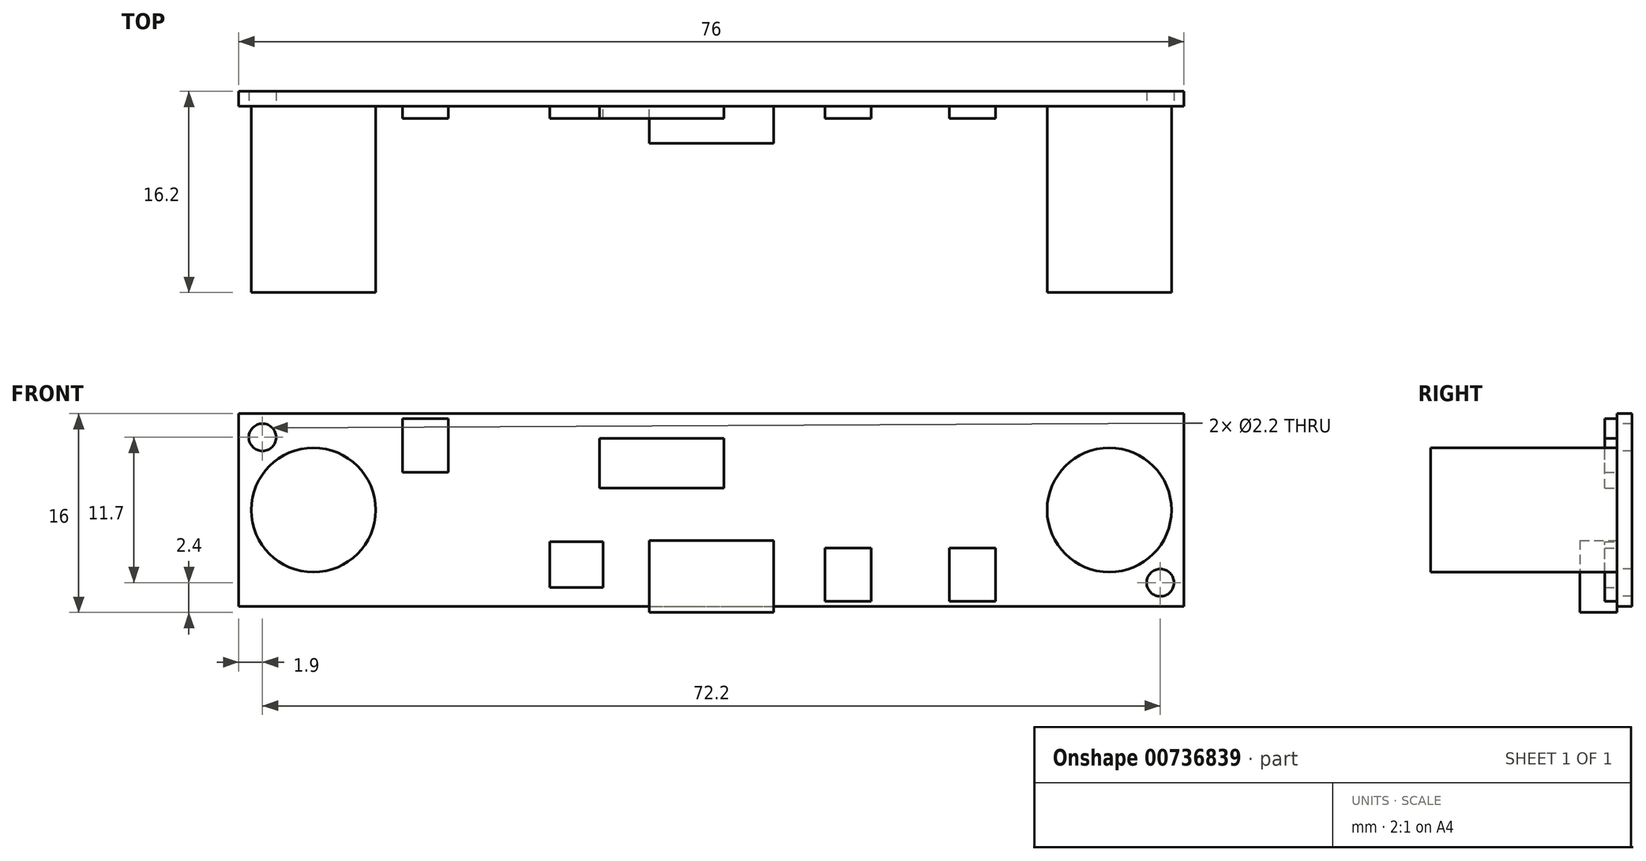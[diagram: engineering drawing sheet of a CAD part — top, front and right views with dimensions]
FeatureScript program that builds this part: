
annotation { "Feature Type Name" : "Feature", "Feature Type Description" : "" }
export const myFeature = defineFeature(function(context is Context, id is Id, definition is map)
    precondition{}
    {
        {
            var Q0;
            Q0=qCreatedBy(makeId("Front.planeOp"),FACE);
            var sketch = newSketch(context, id + "F0", { "sketchPlane" : qUnion([Q0])});
            skLineSegment(sketch, "E0.bottom", {"start": v(-38, 7.75) * mm, "end": v(38, 7.75) * mm});
            skLineSegment(sketch, "E0.top", {"start": v(-38, -7.75) * mm, "end": v(38, -7.75) * mm});
            skLineSegment(sketch, "E0.left", {"start": v(-38, 7.75) * mm, "end": v(-38, -7.75) * mm});
            skLineSegment(sketch, "E0.right", {"start": v(38, 7.75) * mm, "end": v(38, -7.75) * mm});
            skPoint(sketch, "E0.middle", {"position": v(0, 0) * mm});
            skCircle(sketch, "E1", {"center": v(36.1, -5.85) * mm, "radius": 1.1 * mm});
            skCircle(sketch, "E2.1.1", {"center": v(-36.1, 5.85) * mm, "radius": 1.1 * mm});
            skSolve(sketch);
        }
        {
            var Q0;
            Q0=qSketchRegion(id+"F0",true);
            extrude(context, id + "F1", {"entities" : qUnion([Q0]), "oppositeDirection" : true, "depth" : 1.2 * mm});
        }
        {
            var Q0;
            Q0=qCreatedBy(makeId("Front.planeOp"),FACE);
            var sketch = newSketch(context, id + "F2", { "sketchPlane" : qUnion([Q0])});
            skLineSegment(sketch, "E3.bottom", {"start": v(-38, 7.75) * mm, "end": v(38, 7.75) * mm, "construction": true});
            skLineSegment(sketch, "E3.top", {"start": v(-38, -7.75) * mm, "end": v(38, -7.75) * mm, "construction": true});
            skLineSegment(sketch, "E3.left", {"start": v(-38, 7.75) * mm, "end": v(-38, -7.75) * mm, "construction": true});
            skLineSegment(sketch, "E3.right", {"start": v(38, 7.75) * mm, "end": v(38, -7.75) * mm, "construction": true});
            skPoint(sketch, "E3.middle", {"position": v(0, 0) * mm});
            skPoint(sketch, "E4.middle", {"position": v(0, -7.75) * mm});
            skLineSegment(sketch, "E5.bottom", {"start": v(12.85, -7.35) * mm, "end": v(9.15, -7.35) * mm});
            skLineSegment(sketch, "E5.top", {"start": v(12.85, -3.05) * mm, "end": v(9.15, -3.05) * mm});
            skLineSegment(sketch, "E5.left", {"start": v(12.85, -7.35) * mm, "end": v(12.85, -3.05) * mm});
            skLineSegment(sketch, "E5.right", {"start": v(9.15, -7.35) * mm, "end": v(9.15, -3.05) * mm});
            skPoint(sketch, "E5.middle", {"position": v(11, -5.2) * mm});
            skLineSegment(sketch, "E6.bottom", {"start": v(-21.15, 3.05) * mm, "end": v(-24.85, 3.05) * mm});
            skLineSegment(sketch, "E6.top", {"start": v(-21.15, 7.35) * mm, "end": v(-24.85, 7.35) * mm});
            skLineSegment(sketch, "E6.left", {"start": v(-21.15, 3.05) * mm, "end": v(-21.15, 7.35) * mm});
            skLineSegment(sketch, "E6.right", {"start": v(-24.85, 3.05) * mm, "end": v(-24.85, 7.35) * mm});
            skPoint(sketch, "E6.middle", {"position": v(-23, 5.2) * mm});
            skLineSegment(sketch, "E7", {"start": v(16, 2.67) * mm, "end": v(16, -12) * mm, "construction": true});
            skLineSegment(sketch, "E8.MirrorCS", {"start": v(19.15, -7.35) * mm, "end": v(19.15, -3.05) * mm});
            skLineSegment(sketch, "E9.MirrorCS", {"start": v(19.15, -3.05) * mm, "end": v(22.85, -3.05) * mm});
            skLineSegment(sketch, "E10.MirrorCS", {"start": v(22.85, -7.35) * mm, "end": v(22.85, -3.05) * mm});
            skLineSegment(sketch, "E11.MirrorCS", {"start": v(19.15, -7.35) * mm, "end": v(22.85, -7.35) * mm});
            skLineSegment(sketch, "E12.bottom", {"start": v(1, 1.75) * mm, "end": v(-9, 1.75) * mm});
            skLineSegment(sketch, "E12.top", {"start": v(1, 5.75) * mm, "end": v(-9, 5.75) * mm});
            skLineSegment(sketch, "E12.left", {"start": v(1, 1.75) * mm, "end": v(1, 5.75) * mm});
            skLineSegment(sketch, "E12.right", {"start": v(-9, 1.75) * mm, "end": v(-9, 5.75) * mm});
            skPoint(sketch, "E12.middle", {"position": v(-4, 3.75) * mm});
            skLineSegment(sketch, "E13.bottom", {"start": v(-8.7, -6.25) * mm, "end": v(-13, -6.25) * mm});
            skLineSegment(sketch, "E13.top", {"start": v(-8.7, -2.55) * mm, "end": v(-13, -2.55) * mm});
            skLineSegment(sketch, "E13.left", {"start": v(-8.7, -6.25) * mm, "end": v(-8.7, -2.55) * mm});
            skLineSegment(sketch, "E13.right", {"start": v(-13, -6.25) * mm, "end": v(-13, -2.55) * mm});
            skPoint(sketch, "E13.middle", {"position": v(-10.85, -4.4) * mm});
            skSolve(sketch);
        }
        {
            var Q0;
            Q0=qCreatedBy(makeId("Front.planeOp"),FACE);
            var sketch = newSketch(context, id + "F3", { "sketchPlane" : qUnion([Q0])});
            skLineSegment(sketch, "E14.bottom", {"start": v(-38, 7.75) * mm, "end": v(38, 7.75) * mm, "construction": true});
            skLineSegment(sketch, "E14.top", {"start": v(-38, -7.75) * mm, "end": v(38, -7.75) * mm, "construction": true});
            skLineSegment(sketch, "E14.left", {"start": v(-38, 7.75) * mm, "end": v(-38, -7.75) * mm, "construction": true});
            skLineSegment(sketch, "E14.right", {"start": v(38, 7.75) * mm, "end": v(38, -7.75) * mm, "construction": true});
            skCircle(sketch, "E15", {"center": v(32, 0) * mm, "radius": 5 * mm});
            skCircle(sketch, "E16.MirrorC", {"center": v(-32, 0) * mm, "radius": 5 * mm});
            skSolve(sketch);
        }
        {
            var Q0;
            Q0=qSketchRegion(id+"F2",true);
            extrude(context, id + "F4", {"entities" : qUnion([Q0]), "operationType" : NewBodyOperationType.ADD, "depth" : 1 * mm});
        }
        {
            var Q0;
            Q0=qSketchRegion(id+"F3",true);
            extrude(context, id + "F5", {"entities" : qUnion([Q0]), "operationType" : NewBodyOperationType.ADD, "depth" : 15 * mm, "offsetDistance" : 25 * mm});
        }
        {
            var Q0;
            Q0=qCreatedBy(makeId("Front.planeOp"),FACE);
            var sketch = newSketch(context, id + "F6", { "sketchPlane" : qUnion([Q0])});
            skLineSegment(sketch, "E17.bottom", {"start": v(-5, -2.45) * mm, "end": v(5, -2.45) * mm});
            skLineSegment(sketch, "E17.top", {"start": v(-5, -8.25) * mm, "end": v(5, -8.25) * mm});
            skLineSegment(sketch, "E17.left", {"start": v(-5, -2.45) * mm, "end": v(-5, -8.25) * mm});
            skLineSegment(sketch, "E17.right", {"start": v(5, -2.45) * mm, "end": v(5, -8.25) * mm});
            skSolve(sketch);
        }
        {
            var Q0;
            Q0=qSketchRegion(id+"F6",true);
            extrude(context, id + "F7", {"entities" : qUnion([Q0]), "operationType" : NewBodyOperationType.ADD, "depth" : 3 * mm});
        }
    });
